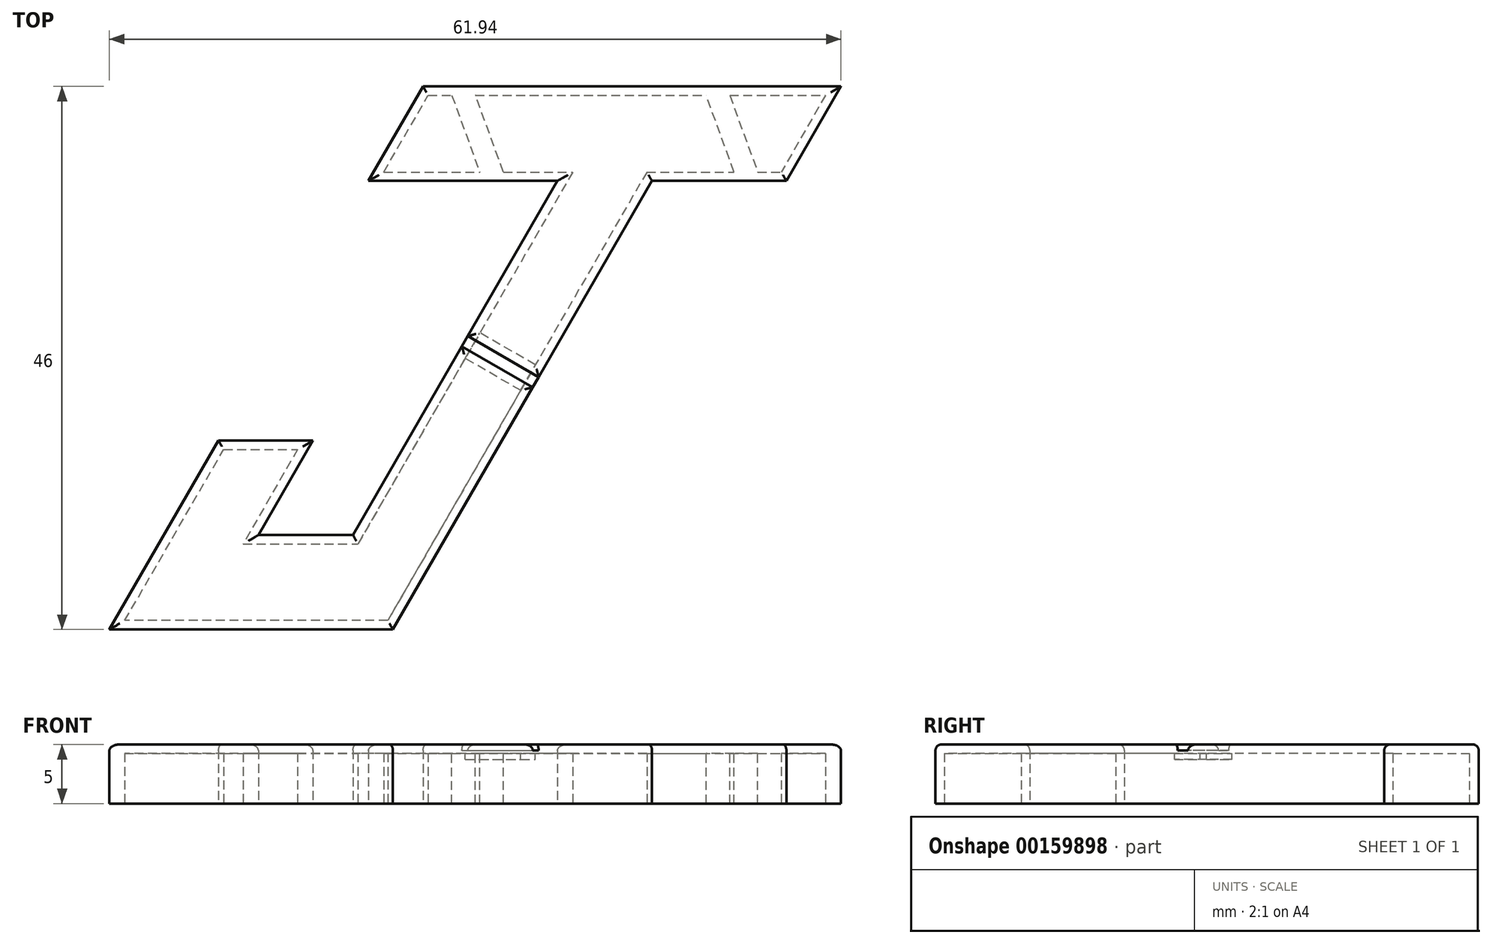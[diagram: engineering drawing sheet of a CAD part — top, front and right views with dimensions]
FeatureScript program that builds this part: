
annotation { "Feature Type Name" : "Feature", "Feature Type Description" : "" }
export const myFeature = defineFeature(function(context is Context, id is Id, definition is map)
    precondition{}
    {
        {
            var Q0;
            Q0=qCreatedBy(makeId("Top.planeOp"),FACE);
            var sketch = newSketch(context, id + "F0", { "sketchPlane" : qUnion([Q0])});
            skLineSegment(sketch, "E0.bottom", {"start": v(4, -30) * mm, "end": v(-4, -30) * mm, "construction": true});
            skLineSegment(sketch, "E0.left", {"start": v(4, -30) * mm, "end": v(4, 30) * mm, "construction": true});
            skLineSegment(sketch, "E0.right", {"start": v(-4, -30) * mm, "end": v(-4, 30) * mm, "construction": true});
            skPoint(sketch, "E0.middle", {"position": v(0, 0) * mm});
            skLineSegment(sketch, "E1.bottom", {"start": v(-20, 30) * mm, "end": v(-4, 30) * mm});
            skLineSegment(sketch, "E1.top", {"start": v(-15.38, 38) * mm, "end": v(20, 38) * mm});
            skLineSegment(sketch, "E1.left", {"start": v(-20, 30) * mm, "end": v(-20, 38) * mm, "construction": true});
            skLineSegment(sketch, "E1.right", {"start": v(20, 30) * mm, "end": v(20, 38) * mm, "construction": true});
            skLineSegment(sketch, "E2.trimOffspring", {"start": v(4, 30) * mm, "end": v(15.38, 30) * mm});
            skLineSegment(sketch, "E3", {"start": v(-4, 30) * mm, "end": v(4, 30) * mm, "construction": true});
            skLineSegment(sketch, "E4", {"start": v(-20, 30) * mm, "end": v(-15.38, 38) * mm});
            skLineSegment(sketch, "E5", {"start": v(20, 38) * mm, "end": v(15.38, 30) * mm});
            skLineSegment(sketch, "E6", {"start": v(-4, 30) * mm, "end": v(-21.32, 0) * mm});
            skLineSegment(sketch, "E7", {"start": v(4, 30) * mm, "end": v(-17.94, -8) * mm});
            skLineSegment(sketch, "E8", {"start": v(0, 0) * mm, "end": v(0, -8) * mm, "construction": true});
            skLineSegment(sketch, "E9", {"start": v(0, -8) * mm, "end": v(-10, -8) * mm, "construction": true});
            skPoint(sketch, "E10.orphan", {"position": v(-13.32, 0) * mm});
            skLineSegment(sketch, "E11", {"start": v(-17.94, -8) * mm, "end": v(-41.94, -8) * mm});
            skLineSegment(sketch, "E12", {"start": v(-41.94, -8) * mm, "end": v(-32.7, 8) * mm});
            skLineSegment(sketch, "E13", {"start": v(-32.7, 8) * mm, "end": v(-24.7, 8) * mm});
            skLineSegment(sketch, "E14", {"start": v(-24.7, 8) * mm, "end": v(-29.32, 0) * mm});
            skLineSegment(sketch, "E15", {"start": v(-29.32, 0) * mm, "end": v(-21.32, 0) * mm});
            skSolve(sketch);
        }
        {
            var Q0;
            Q0=makeQuery(id+"F0.imprint","IMPRINT",FACE,{"disambiguationData":[TD([[makeQuery(id+"F0.imprint","IMPRINT",EDGE,{"derivedFrom":sQuery(id+"F0.wireOp",EDGE,"E1.bottom")}),1.0]])]});
            extrude(context, id + "F1", {"entities" : qUnion([Q0]), "depth" : 5 * mm});
        }
        {
            var Q0;
            Q0=qCreatedBy(makeId("Right.planeOp"),FACE);
            var sketch = newSketch(context, id + "F2", { "sketchPlane" : qUnion([Q0])});
            skLineSegment(sketch, "E16", {"start": v(38, 0) * mm, "end": v(-8, 0) * mm, "construction": true});
            skLineSegment(sketch, "E17", {"start": v(9, 0) * mm, "end": v(9, 4.5) * mm});
            skSolve(sketch);
        }
        {
            var Q0;
            Q0=makeQuery(id+"F1.opExtrude","SWEPT_FACE",FACE,{"disambiguationData":[OSD([sQuery(id+"F0.wireOp",EDGE,"E7")])]});
            cPlane(context, id + "F3", {"entities" : qUnion([Q0]), "cplaneType" : CPlaneType.OFFSET, "offset" : 25 * mm, "width" : 150 * mm, "height" : 150 * mm});
        }
        {
            var Q0;
            Q0=qCreatedBy(id+"F3.planeOp",FACE);
            var sketch = newSketch(context, id + "F4", { "sketchPlane" : qUnion([Q0])});
            skLineSegment(sketch, "E18.bottom", {"start": v(7.8, 4.5) * mm, "end": v(8.8, 4.5) * mm});
            skLineSegment(sketch, "E18.top", {"start": v(7.8, 9.88) * mm, "end": v(8.8, 9.88) * mm});
            skLineSegment(sketch, "E18.left", {"start": v(7.8, 4.5) * mm, "end": v(7.8, 9.88) * mm});
            skLineSegment(sketch, "E18.right", {"start": v(8.8, 4.5) * mm, "end": v(8.8, 9.88) * mm});
            skSolve(sketch);
        }
        {
            var Q0;
            Q0=makeQuery(id+"F4.imprint","IMPRINT",FACE,{"disambiguationData":[TD([[makeQuery(id+"F4.imprint","IMPRINT",EDGE,{"derivedFrom":sQuery(id+"F4.wireOp",EDGE,"E18.bottom")}),1.0]])]});
            extrude(context, id + "F5", {"entities" : qUnion([Q0]), "operationType" : NewBodyOperationType.REMOVE, "oppositeDirection" : true, "depth" : 100 * mm});
        }
        {
            var Q0;
            Q0=makeQuery(id+"F1.opExtrude","CAP_FACE",FACE,{"disambiguationData":[OSD([sQuery(id+"F0.wireOp",EDGE,"E1.bottom"),sQuery(id+"F0.wireOp",EDGE,"E1.top"),sQuery(id+"F0.wireOp",EDGE,"E2.trimOffspring"),sQuery(id+"F0.wireOp",EDGE,"E4"),sQuery(id+"F0.wireOp",EDGE,"E5"),sQuery(id+"F0.wireOp",EDGE,"E6"),sQuery(id+"F0.wireOp",EDGE,"E7"),sQuery(id+"F0.wireOp",EDGE,"E11"),sQuery(id+"F0.wireOp",EDGE,"E12"),sQuery(id+"F0.wireOp",EDGE,"E13"),sQuery(id+"F0.wireOp",EDGE,"E14"),sQuery(id+"F0.wireOp",EDGE,"E15")])],"isStart":true});
            shell(context, id + "F6", {"entities" : qUnion([Q0]), "thickness" : .75 * mm});
        }
        {
            var Q0;
            {var subQ0=sQuery(id+"F0.wireOp",EDGE,"E7");var subQ1=sQuery(id+"F0.wireOp",EDGE,"E2.trimOffspring");Q0=makeQuery(id+"F5.boolean.opBoolean","SPLIT",EDGE,{"disambiguationData":[TD([makeQuery(id+"F1.opExtrude","SWEPT_FACE",FACE,{"disambiguationData":[OSD([subQ1])]})])],"derivedFrom":makeQuery(id+"F1.opExtrude","CAP_EDGE",EDGE,{"disambiguationData":[OSD([subQ0])],"isStart":false})});}
            var Q1;
            Q1=makeQuery(id+"F1.opExtrude","CAP_EDGE",EDGE,{"disambiguationData":[OSD([sQuery(id+"F0.wireOp",EDGE,"E2.trimOffspring")])],"isStart":false});
            var Q2;
            Q2=makeQuery(id+"F1.opExtrude","CAP_EDGE",EDGE,{"disambiguationData":[OSD([sQuery(id+"F0.wireOp",EDGE,"E5")])],"isStart":false});
            var Q3;
            Q3=makeQuery(id+"F1.opExtrude","CAP_EDGE",EDGE,{"disambiguationData":[OSD([sQuery(id+"F0.wireOp",EDGE,"E1.top")])],"isStart":false});
            var Q4;
            Q4=makeQuery(id+"F1.opExtrude","CAP_EDGE",EDGE,{"disambiguationData":[OSD([sQuery(id+"F0.wireOp",EDGE,"E4")])],"isStart":false});
            var Q5;
            Q5=makeQuery(id+"F1.opExtrude","CAP_EDGE",EDGE,{"disambiguationData":[OSD([sQuery(id+"F0.wireOp",EDGE,"E1.bottom")])],"isStart":false});
            var Q6;
            {var subQ0=sQuery(id+"F0.wireOp",EDGE,"E1.bottom");var subQ1=sQuery(id+"F0.wireOp",EDGE,"E6");Q6=makeQuery(id+"F5.boolean.opBoolean","SPLIT",EDGE,{"disambiguationData":[TD([makeQuery(id+"F1.opExtrude","SWEPT_FACE",FACE,{"disambiguationData":[OSD([subQ0])]})])],"derivedFrom":makeQuery(id+"F1.opExtrude","CAP_EDGE",EDGE,{"disambiguationData":[OSD([subQ1])],"isStart":false})});}
            var Q7;
            Q7=makeQuery(id+"F5.boolean.opBoolean","INTERSECT",EDGE,{"derivedFrom":[makeQuery(id+"F1.opExtrude","CAP_FACE",FACE,{"disambiguationData":[OSD([sQuery(id+"F0.wireOp",EDGE,"E1.bottom"),sQuery(id+"F0.wireOp",EDGE,"E1.top"),sQuery(id+"F0.wireOp",EDGE,"E2.trimOffspring"),sQuery(id+"F0.wireOp",EDGE,"E4"),sQuery(id+"F0.wireOp",EDGE,"E5"),sQuery(id+"F0.wireOp",EDGE,"E6"),sQuery(id+"F0.wireOp",EDGE,"E7"),sQuery(id+"F0.wireOp",EDGE,"E11"),sQuery(id+"F0.wireOp",EDGE,"E12"),sQuery(id+"F0.wireOp",EDGE,"E13"),sQuery(id+"F0.wireOp",EDGE,"E14"),sQuery(id+"F0.wireOp",EDGE,"E15")])],"isStart":false}),makeQuery(id+"F5.opExtrude","SWEPT_FACE",FACE,{"disambiguationData":[OSD([sQuery(id+"F4.wireOp",EDGE,"E18.right")])]})]});
            var Q8;
            {var subQ0=sQuery(id+"F0.wireOp",EDGE,"E15");var subQ1=sQuery(id+"F0.wireOp",EDGE,"E6");Q8=makeQuery(id+"F5.boolean.opBoolean","SPLIT",EDGE,{"disambiguationData":[TD([makeQuery(id+"F1.opExtrude","SWEPT_FACE",FACE,{"disambiguationData":[OSD([subQ0])]})])],"derivedFrom":makeQuery(id+"F1.opExtrude","CAP_EDGE",EDGE,{"disambiguationData":[OSD([subQ1])],"isStart":false})});}
            var Q9;
            Q9=makeQuery(id+"F1.opExtrude","CAP_EDGE",EDGE,{"disambiguationData":[OSD([sQuery(id+"F0.wireOp",EDGE,"E15")])],"isStart":false});
            var Q10;
            Q10=makeQuery(id+"F1.opExtrude","CAP_EDGE",EDGE,{"disambiguationData":[OSD([sQuery(id+"F0.wireOp",EDGE,"E14")])],"isStart":false});
            var Q11;
            Q11=makeQuery(id+"F1.opExtrude","CAP_EDGE",EDGE,{"disambiguationData":[OSD([sQuery(id+"F0.wireOp",EDGE,"E13")])],"isStart":false});
            var Q12;
            Q12=makeQuery(id+"F1.opExtrude","CAP_EDGE",EDGE,{"disambiguationData":[OSD([sQuery(id+"F0.wireOp",EDGE,"E12")])],"isStart":false});
            var Q13;
            Q13=makeQuery(id+"F1.opExtrude","CAP_EDGE",EDGE,{"disambiguationData":[OSD([sQuery(id+"F0.wireOp",EDGE,"E11")])],"isStart":false});
            var Q14;
            {var subQ0=sQuery(id+"F0.wireOp",EDGE,"E11");var subQ1=sQuery(id+"F0.wireOp",EDGE,"E7");Q14=makeQuery(id+"F5.boolean.opBoolean","SPLIT",EDGE,{"disambiguationData":[TD([makeQuery(id+"F1.opExtrude","SWEPT_FACE",FACE,{"disambiguationData":[OSD([subQ0])]})])],"derivedFrom":makeQuery(id+"F1.opExtrude","CAP_EDGE",EDGE,{"disambiguationData":[OSD([subQ1])],"isStart":false})});}
            var Q15;
            Q15=makeQuery(id+"F5.boolean.opBoolean","INTERSECT",EDGE,{"derivedFrom":[makeQuery(id+"F1.opExtrude","CAP_FACE",FACE,{"disambiguationData":[OSD([sQuery(id+"F0.wireOp",EDGE,"E1.bottom"),sQuery(id+"F0.wireOp",EDGE,"E1.top"),sQuery(id+"F0.wireOp",EDGE,"E2.trimOffspring"),sQuery(id+"F0.wireOp",EDGE,"E4"),sQuery(id+"F0.wireOp",EDGE,"E5"),sQuery(id+"F0.wireOp",EDGE,"E6"),sQuery(id+"F0.wireOp",EDGE,"E7"),sQuery(id+"F0.wireOp",EDGE,"E11"),sQuery(id+"F0.wireOp",EDGE,"E12"),sQuery(id+"F0.wireOp",EDGE,"E13"),sQuery(id+"F0.wireOp",EDGE,"E14"),sQuery(id+"F0.wireOp",EDGE,"E15")])],"isStart":false}),makeQuery(id+"F5.opExtrude","SWEPT_FACE",FACE,{"disambiguationData":[OSD([sQuery(id+"F4.wireOp",EDGE,"E18.left")])]})]});
            fillet(context, id + "F7", {"entities" : qUnion([Q0, Q1, Q2, Q3, Q4, Q5, Q6, Q7, Q8, Q9, Q10, Q11, Q12, Q13, Q14, Q15]), "radius" : .5 * mm, "tangentPropagation" : true, "allowEdgeOverflow" : false});
        }
        {
            var Q0;
            {var subQ0=sQuery(id+"F0.wireOp",EDGE,"E4");var subQ1=sQuery(id+"F0.wireOp",EDGE,"E2.trimOffspring");var subQ2=sQuery(id+"F0.wireOp",EDGE,"E1.top");var subQ3=sQuery(id+"F0.wireOp",EDGE,"E1.bottom");var subQ4=sQuery(id+"F0.wireOp",EDGE,"E5");var subQ5=sQuery(id+"F0.wireOp",EDGE,"E6");var subQ6=sQuery(id+"F0.wireOp",EDGE,"E7");var subQ7=sQuery(id+"F0.wireOp",EDGE,"E15");var subQ8=sQuery(id+"F0.wireOp",EDGE,"E14");var subQ9=sQuery(id+"F0.wireOp",EDGE,"E13");var subQ10=sQuery(id+"F0.wireOp",EDGE,"E12");var subQ11=sQuery(id+"F0.wireOp",EDGE,"E11");Q0=makeQuery(id+"F6.opShell","OFFSET_FACE",FACE,{"disambiguationData":[OSD([subQ3,subQ2,subQ1,subQ0,subQ4,subQ5,subQ6,subQ11,subQ10,subQ9,subQ8,subQ7]),TDD([makeQuery(id+"F5.boolean.opBoolean","SPLIT",FACE,{"disambiguationData":[TD([makeQuery(id+"F1.opExtrude","SWEPT_FACE",FACE,{"disambiguationData":[OSD([subQ3])]})])],"derivedFrom":makeQuery(id+"F1.opExtrude","CAP_FACE",FACE,{"disambiguationData":[OSD([subQ3,subQ2,subQ1,subQ0,subQ4,subQ5,subQ6,subQ11,subQ10,subQ9,subQ8,subQ7])],"isStart":false})})])]});}
            var sketch = newSketch(context, id + "F8", { "sketchPlane" : qUnion([Q0])});
            skLineSegment(sketch, "E19", {"start": v(-12.95, -37.25) * mm, "end": v(-10.58, -30.75) * mm});
            skLineSegment(sketch, "E20", {"start": v(-8.58, -30.75) * mm, "end": v(-10.95, -37.25) * mm});
            skLineSegment(sketch, "E21", {"start": v(-12.95, -37.25) * mm, "end": v(-10.95, -37.25) * mm});
            skLineSegment(sketch, "E22", {"start": v(-10.58, -30.75) * mm, "end": v(-8.58, -30.75) * mm});
            skLineSegment(sketch, "E23", {"start": v(12.95, -30.75) * mm, "end": v(10.58, -37.25) * mm});
            skLineSegment(sketch, "E24", {"start": v(10.95, -30.75) * mm, "end": v(8.58, -37.25) * mm});
            skLineSegment(sketch, "E25", {"start": v(8.58, -37.25) * mm, "end": v(10.58, -37.25) * mm});
            skLineSegment(sketch, "E26", {"start": v(10.95, -30.75) * mm, "end": v(12.95, -30.75) * mm});
            skSolve(sketch);
        }
        {
            var Q0;
            Q0=makeQuery(id+"F8.imprint","IMPRINT",FACE,{"disambiguationData":[TD([[makeQuery(id+"F8.imprint","IMPRINT",EDGE,{"derivedFrom":sQuery(id+"F8.wireOp",EDGE,"E19")}),-1.0]])]});
            var Q1;
            Q1=makeQuery(id+"F8.imprint","IMPRINT",FACE,{"disambiguationData":[TD([[makeQuery(id+"F8.imprint","IMPRINT",EDGE,{"derivedFrom":sQuery(id+"F8.wireOp",EDGE,"E23")}),-1.0]])]});
            var Q2;
            Q2=makeQuery(id+"F1.opExtrude","CAP_FACE",FACE,{"disambiguationData":[OSD([sQuery(id+"F0.wireOp",EDGE,"E1.bottom"),sQuery(id+"F0.wireOp",EDGE,"E1.top"),sQuery(id+"F0.wireOp",EDGE,"E2.trimOffspring"),sQuery(id+"F0.wireOp",EDGE,"E4"),sQuery(id+"F0.wireOp",EDGE,"E5"),sQuery(id+"F0.wireOp",EDGE,"E6"),sQuery(id+"F0.wireOp",EDGE,"E7"),sQuery(id+"F0.wireOp",EDGE,"E11"),sQuery(id+"F0.wireOp",EDGE,"E12"),sQuery(id+"F0.wireOp",EDGE,"E13"),sQuery(id+"F0.wireOp",EDGE,"E14"),sQuery(id+"F0.wireOp",EDGE,"E15")])],"isStart":true});
            extrude(context, id + "F9", {"entities" : qUnion([Q0, Q1]), "operationType" : NewBodyOperationType.ADD, "endBound" : BoundingType.UP_TO_SURFACE, "endBoundEntityFace" : qUnion([Q2]), "depth" : 25 * mm});
        }
    });
